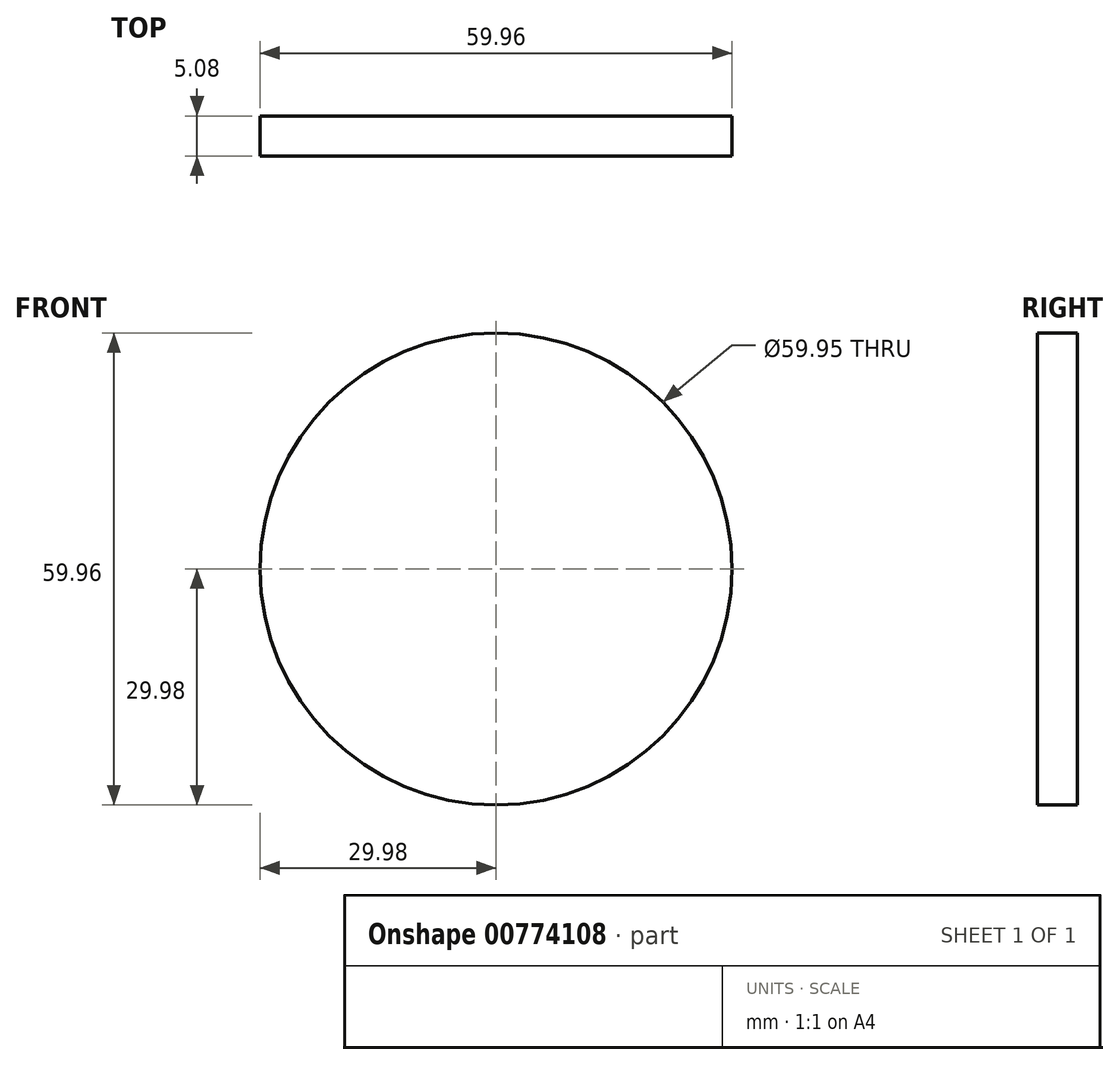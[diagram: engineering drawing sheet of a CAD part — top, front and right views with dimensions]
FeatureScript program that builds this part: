
annotation { "Feature Type Name" : "Feature", "Feature Type Description" : "" }
export const myFeature = defineFeature(function(context is Context, id is Id, definition is map)
    precondition{}
    {
        {
            var Q0;
            Q0=qCreatedBy(makeId("Front.planeOp"),FACE);
            var sketch = newSketch(context, id + "F0", { "sketchPlane" : qUnion([Q0])});
            skCircle(sketch, "E0", {"center": v(0, 0) * mm, "radius": 29.98 * mm});
            skSolve(sketch);
        }
        {
            var Q0;
            Q0=sQuery(id+"F0.wireOp",EDGE,"E0");
            extrude(context, id + "F1", {"bodyType" : ToolBodyType.SURFACE, "surfaceEntities" : qUnion([Q0]), "depth" : -5.08 * mm, "offsetDistance" : 25.4 * mm});
        }
    });
